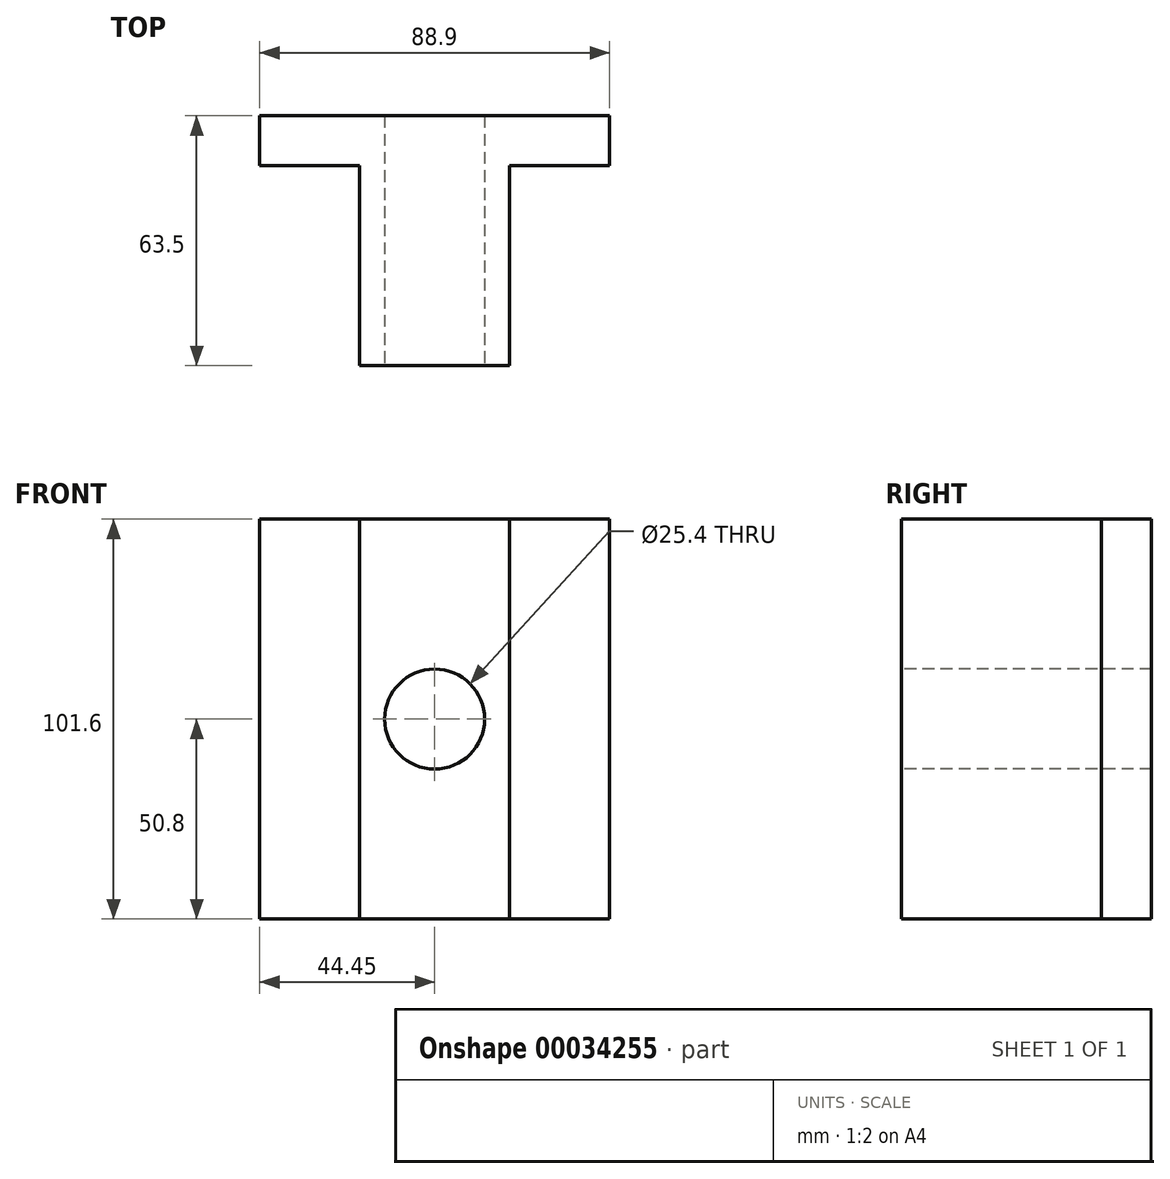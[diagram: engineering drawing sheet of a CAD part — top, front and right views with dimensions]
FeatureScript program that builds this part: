
annotation { "Feature Type Name" : "Feature", "Feature Type Description" : "" }
export const myFeature = defineFeature(function(context is Context, id is Id, definition is map)
    precondition{}
    {
        {
            var Q0;
            Q0=qCreatedBy(makeId("Top.planeOp"),FACE);
            var sketch = newSketch(context, id + "F0", { "sketchPlane" : qUnion([Q0])});
            skLineSegment(sketch, "E0.bottom", {"start": v(0, 0) * mm, "end": v(-88.9, 0) * mm});
            skLineSegment(sketch, "E0.top", {"start": v(0, -12.7) * mm, "end": v(-25.4, -12.7) * mm});
            skLineSegment(sketch, "E0.left", {"start": v(0, 0) * mm, "end": v(0, -12.7) * mm});
            skLineSegment(sketch, "E0.right", {"start": v(-88.9, 0) * mm, "end": v(-88.9, -12.7) * mm});
            skLineSegment(sketch, "E1.top", {"start": v(-63.5, -63.5) * mm, "end": v(-25.4, -63.5) * mm});
            skLineSegment(sketch, "E1.left", {"start": v(-63.5, -12.7) * mm, "end": v(-63.5, -63.5) * mm});
            skLineSegment(sketch, "E1.right", {"start": v(-25.4, -12.7) * mm, "end": v(-25.4, -63.5) * mm});
            skLineSegment(sketch, "E2.trimOffspring", {"start": v(-63.5, -12.7) * mm, "end": v(-88.9, -12.7) * mm});
            skSolve(sketch);
        }
        {
            var Q0;
            Q0=makeQuery(id+"F0.imprint","IMPRINT",FACE,{"disambiguationData":[TD([[makeQuery(id+"F0.imprint","IMPRINT",EDGE,{"derivedFrom":sQuery(id+"F0.wireOp",EDGE,"E0.bottom")}),1.0]])]});
            extrude(context, id + "F1", {"entities" : qUnion([Q0]), "depth" : 101.6 * mm});
        }
        {
            var Q0;
            Q0=makeQuery(id+"F1.opExtrude","SWEPT_FACE",FACE,{"disambiguationData":[OSD([sQuery(id+"F0.wireOp",EDGE,"E1.top")])]});
            var sketch = newSketch(context, id + "F2", { "sketchPlane" : qUnion([Q0])});
            skCircle(sketch, "E3", {"center": v(-44.45, 50.8) * mm, "radius": 12.7 * mm});
            skSolve(sketch);
        }
        {
            var Q0;
            Q0=makeQuery(id+"F2.imprint","IMPRINT",FACE,{"disambiguationData":[TD([[makeQuery(id+"F2.imprint","IMPRINT",EDGE,{"derivedFrom":sQuery(id+"F2.wireOp",EDGE,"E3")}),1.0]])]});
            extrude(context, id + "F3", {"entities" : qUnion([Q0]), "operationType" : NewBodyOperationType.REMOVE, "endBound" : BoundingType.THROUGH_ALL, "oppositeDirection" : true, "depth" : 25.4 * mm});
        }
    });
